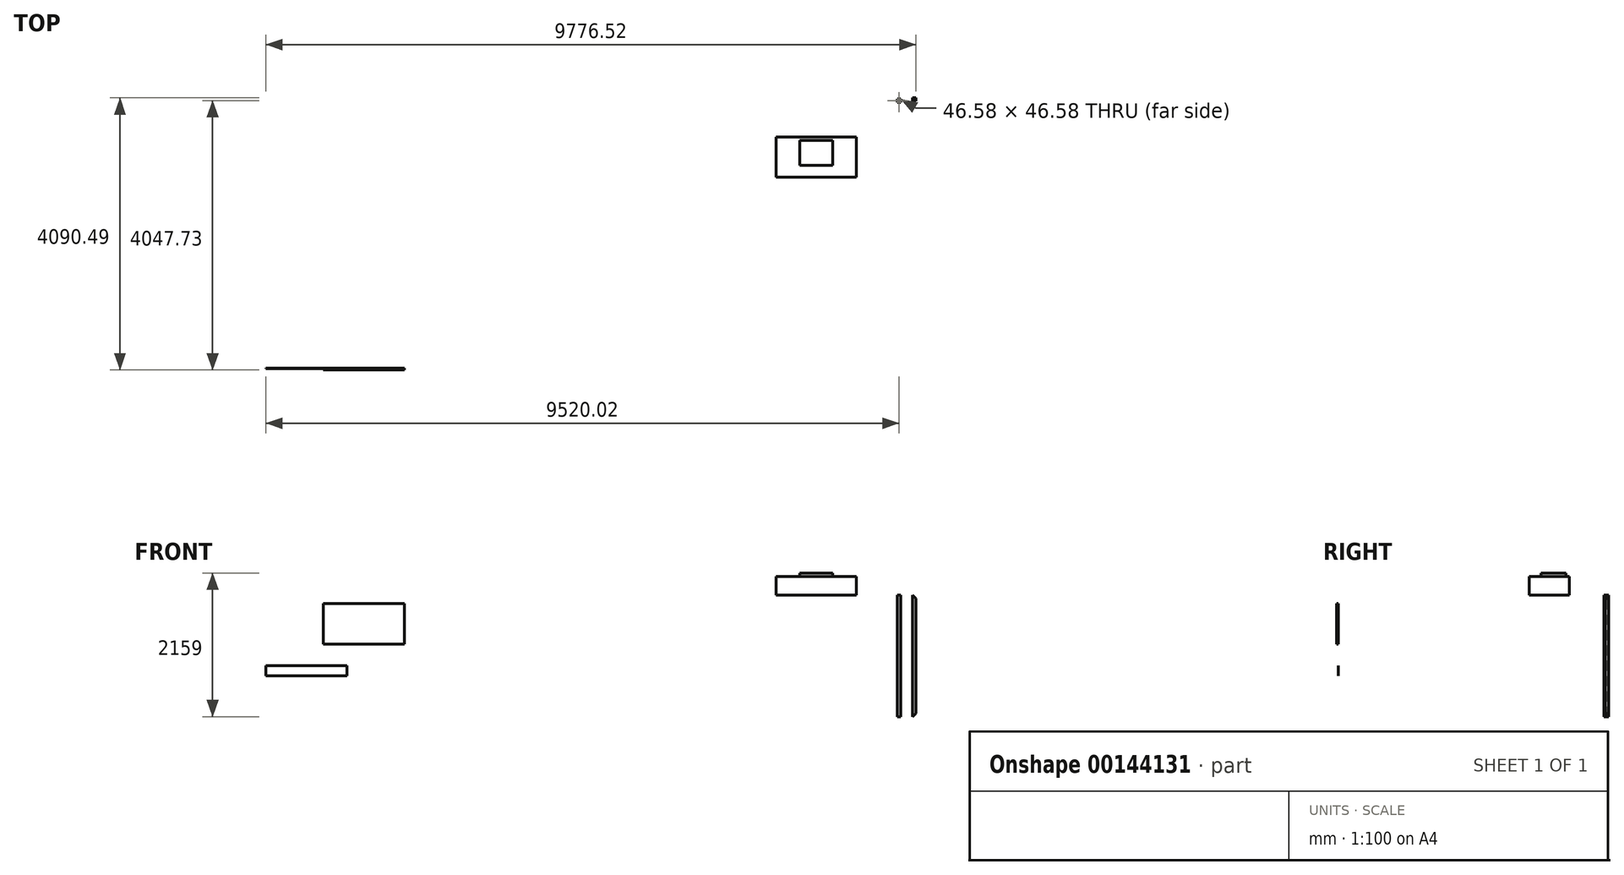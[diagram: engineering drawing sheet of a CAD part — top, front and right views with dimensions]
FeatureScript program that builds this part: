
annotation { "Feature Type Name" : "Feature", "Feature Type Description" : "" }
export const myFeature = defineFeature(function(context is Context, id is Id, definition is map)
    precondition{}
    {
        {
            var Q0;
            Q0=qCreatedBy(makeId("Top.planeOp"),FACE);
            var sketch = newSketch(context, id + "F0", { "sketchPlane" : qUnion([Q0])});
            skLineSegment(sketch, "E0.bottom", {"start": v(2392.46, 2874.24) * mm, "end": v(3602.13, 2874.24) * mm});
            skLineSegment(sketch, "E0.top", {"start": v(2392.46, 3474.32) * mm, "end": v(3602.13, 3474.32) * mm});
            skLineSegment(sketch, "E0.left", {"start": v(2392.46, 2874.24) * mm, "end": v(2392.46, 3474.32) * mm});
            skLineSegment(sketch, "E0.right", {"start": v(3602.13, 2874.24) * mm, "end": v(3602.13, 3474.32) * mm});
            skSolve(sketch);
        }
        {
            var Q0;
            Q0 = qSketchRegion(id + "F0", true);
            extrude(context, id + "F1", {"entities" : qUnion([Q0]), "depth" : 279.4 * mm});
        }
        {
            var Q0;
            Q0=makeQuery(id+"F1.opExtrude","CAP_FACE",FACE,{"disambiguationData":[OSD([sQuery(id+"F0.wireOp",EDGE,"E0.bottom"),sQuery(id+"F0.wireOp",EDGE,"E0.top"),sQuery(id+"F0.wireOp",EDGE,"E0.left"),sQuery(id+"F0.wireOp",EDGE,"E0.right")])],"isStart":false});
            var sketch = newSketch(context, id + "F2", { "sketchPlane" : qUnion([Q0])});
            skLineSegment(sketch, "E1.bottom", {"start": v(2748.06, 3423.52) * mm, "end": v(3246.53, 3423.52) * mm});
            skLineSegment(sketch, "E1.top", {"start": v(2748.06, 3052.04) * mm, "end": v(3246.53, 3052.04) * mm});
            skLineSegment(sketch, "E1.left", {"start": v(2748.06, 3423.52) * mm, "end": v(2748.06, 3052.04) * mm});
            skLineSegment(sketch, "E1.right", {"start": v(3246.53, 3423.52) * mm, "end": v(3246.53, 3052.04) * mm});
            skSolve(sketch);
        }
        {
            var Q0;
            Q0 = qSketchRegion(id + "F2", true);
            extrude(context, id + "F3", {"entities" : qUnion([Q0]), "operationType" : NewBodyOperationType.ADD, "depth" : 50.8 * mm});
        }
        {
            var Q0;
            Q0=qCreatedBy(makeId("Top.planeOp"),FACE);
            var sketch = newSketch(context, id + "F4", { "sketchPlane" : qUnion([Q0])});
            skLineSegment(sketch, "E2.bottom", {"start": v(4215.26, 4047.73) * mm, "end": v(4266.06, 4047.73) * mm});
            skLineSegment(sketch, "E2.top", {"start": v(4215.26, 3996.93) * mm, "end": v(4266.06, 3996.93) * mm});
            skLineSegment(sketch, "E2.left", {"start": v(4215.26, 4047.73) * mm, "end": v(4215.26, 3996.93) * mm});
            skLineSegment(sketch, "E2.right", {"start": v(4266.06, 4047.73) * mm, "end": v(4266.06, 3996.93) * mm});
            skLineSegment(sketch, "E3.bottom", {"start": v(4217.37, 4045.62) * mm, "end": v(4263.95, 4045.62) * mm});
            skLineSegment(sketch, "E3.top", {"start": v(4217.37, 3999.04) * mm, "end": v(4263.95, 3999.04) * mm});
            skLineSegment(sketch, "E3.left", {"start": v(4217.37, 4045.62) * mm, "end": v(4217.37, 3999.04) * mm});
            skLineSegment(sketch, "E3.right", {"start": v(4263.95, 4045.62) * mm, "end": v(4263.95, 3999.04) * mm});
            skSolve(sketch);
        }
        {
            var Q0;
            Q0 = qSketchRegion(id + "F4", true);
            extrude(context, id + "F5", {"entities" : qUnion([Q0]), "oppositeDirection" : true, "depth" : 1828.8 * mm});
        }
        {
            var Q0;
            Q0=qCreatedBy(makeId("Top.planeOp"),FACE);
            var sketch = newSketch(context, id + "F6", { "sketchPlane" : qUnion([Q0])});
            skLineSegment(sketch, "E4.bottom", {"start": v(4446.36, 4065.09) * mm, "end": v(4497.16, 4065.09) * mm});
            skLineSegment(sketch, "E4.top", {"start": v(4446.36, 4014.29) * mm, "end": v(4497.16, 4014.29) * mm});
            skLineSegment(sketch, "E4.left", {"start": v(4446.36, 4065.09) * mm, "end": v(4446.36, 4014.29) * mm});
            skLineSegment(sketch, "E4.right", {"start": v(4497.16, 4065.09) * mm, "end": v(4497.16, 4014.29) * mm});
            skLineSegment(sketch, "E5.bottom", {"start": v(4448.47, 4062.98) * mm, "end": v(4495.06, 4062.98) * mm});
            skLineSegment(sketch, "E5.top", {"start": v(4448.47, 4016.4) * mm, "end": v(4495.06, 4016.4) * mm});
            skLineSegment(sketch, "E5.left", {"start": v(4448.47, 4062.98) * mm, "end": v(4448.47, 4016.4) * mm});
            skLineSegment(sketch, "E5.right", {"start": v(4495.06, 4062.98) * mm, "end": v(4495.06, 4016.4) * mm});
            skSolve(sketch);
        }
        {
            var Q0;
            Q0 = qSketchRegion(id + "F6", true);
            extrude(context, id + "F7", {"entities" : qUnion([Q0]), "oppositeDirection" : true, "depth" : 1828.8 * mm});
        }
        {
            var Q0;
            Q0=makeQuery(id+"F7.opExtrude","SWEPT_FACE",FACE,{"disambiguationData":[OSD([sQuery(id+"F6.wireOp",EDGE,"E4.top")])]});
            var sketch = newSketch(context, id + "F8", { "sketchPlane" : qUnion([Q0])});
            skLineSegment(sketch, "E6", {"start": v(4446.36, 0) * mm, "end": v(4497.16, -50.8) * mm});
            skLineSegment(sketch, "E7", {"start": v(4497.16, -50.8) * mm, "end": v(4497.16, 0) * mm});
            skLineSegment(sketch, "E8", {"start": v(4497.16, 0) * mm, "end": v(4446.36, 0) * mm});
            skLineSegment(sketch, "E9", {"start": v(4446.36, -1828.8) * mm, "end": v(4497.16, -1778) * mm});
            skLineSegment(sketch, "E10", {"start": v(4497.16, -1778) * mm, "end": v(4497.16, -1828.8) * mm});
            skLineSegment(sketch, "E11", {"start": v(4497.16, -1828.8) * mm, "end": v(4446.36, -1828.8) * mm});
            skSolve(sketch);
        }
        {
            var Q0;
            Q0 = qSketchRegion(id + "F8", true);
            extrude(context, id + "F9", {"entities" : qUnion([Q0]), "operationType" : NewBodyOperationType.REMOVE, "endBound" : BoundingType.THROUGH_ALL, "oppositeDirection" : true, "depth" : 25.4 * mm});
        }
        {
            var Q0;
            Q0=qCreatedBy(makeId("Front.planeOp"),FACE);
            var sketch = newSketch(context, id + "F10", { "sketchPlane" : qUnion([Q0])});
            skLineSegment(sketch, "E12.bottom", {"start": v(-4413.08, -126.75) * mm, "end": v(-3193.88, -126.75) * mm});
            skLineSegment(sketch, "E12.top", {"start": v(-4413.08, -736.35) * mm, "end": v(-3193.88, -736.35) * mm});
            skLineSegment(sketch, "E12.left", {"start": v(-4413.08, -126.75) * mm, "end": v(-4413.08, -736.35) * mm});
            skLineSegment(sketch, "E12.right", {"start": v(-3193.88, -126.75) * mm, "end": v(-3193.88, -736.35) * mm});
            skSolve(sketch);
        }
        {
            var Q0;
            Q0 = qSketchRegion(id + "F10", true);
            extrude(context, id + "F11", {"entities" : qUnion([Q0]), "depth" : 25.4 * mm});
        }
        {
            var Q0;
            Q0=qCreatedBy(makeId("Front.planeOp"),FACE);
            var sketch = newSketch(context, id + "F12", { "sketchPlane" : qUnion([Q0])});
            skLineSegment(sketch, "E13.bottom", {"start": v(-5279.36, -1062.63) * mm, "end": v(-4060.16, -1062.63) * mm});
            skLineSegment(sketch, "E13.top", {"start": v(-5279.36, -1215.03) * mm, "end": v(-4060.16, -1215.03) * mm});
            skLineSegment(sketch, "E13.left", {"start": v(-5279.36, -1062.63) * mm, "end": v(-5279.36, -1215.03) * mm});
            skLineSegment(sketch, "E13.right", {"start": v(-4060.16, -1062.63) * mm, "end": v(-4060.16, -1215.03) * mm});
            skSolve(sketch);
        }
        {
            var Q0;
            Q0 = qSketchRegion(id + "F12", true);
            extrude(context, id + "F13", {"entities" : qUnion([Q0]), "depth" : 0.89 * mm});
        }
    });
